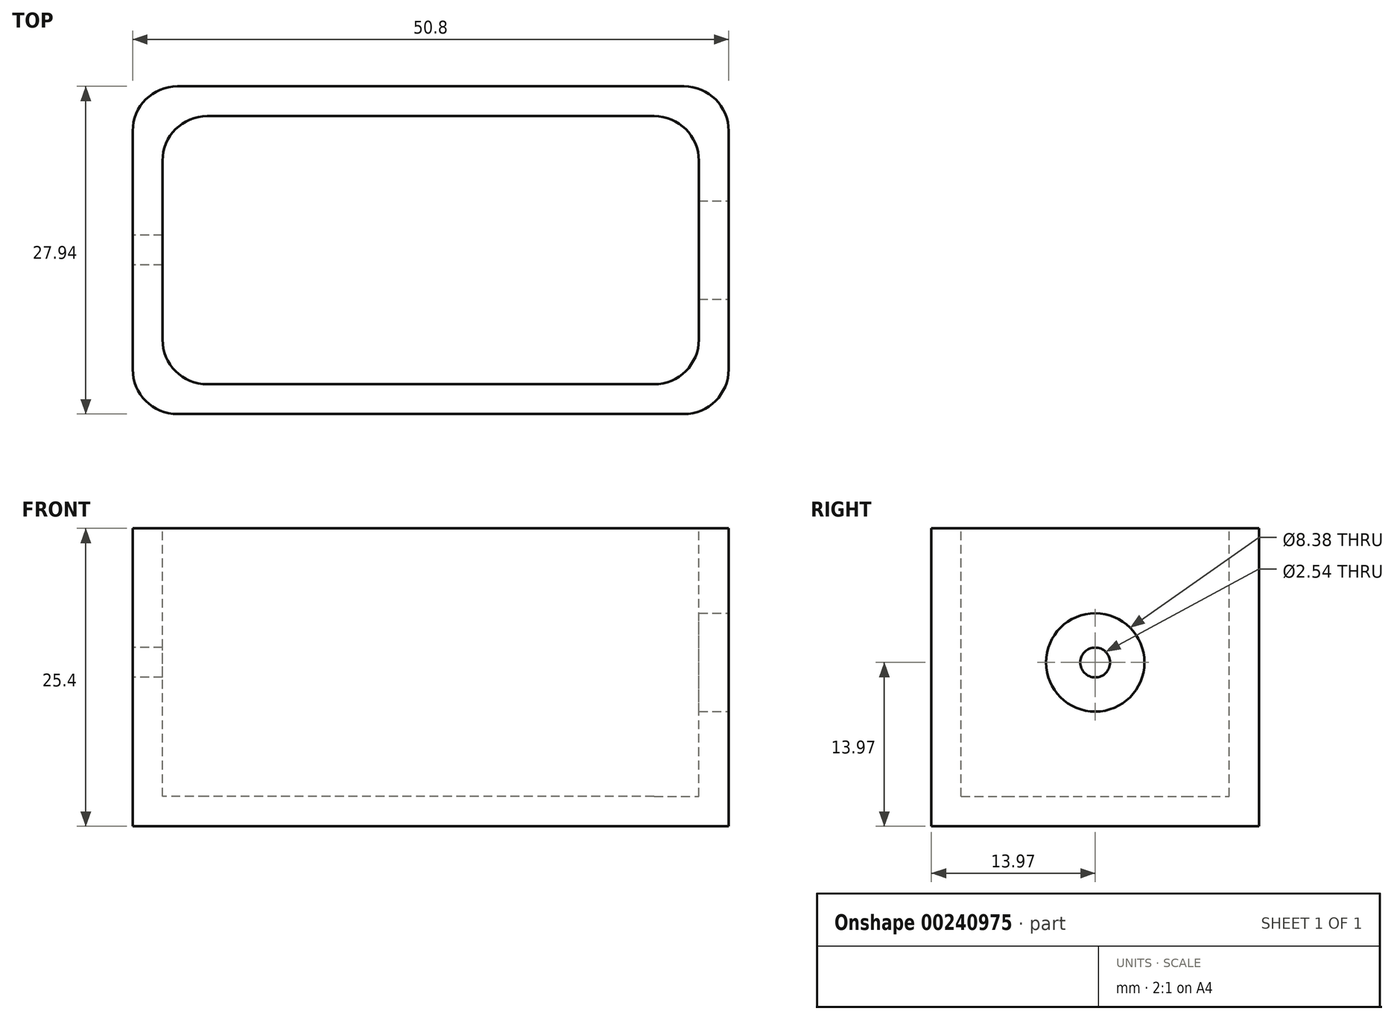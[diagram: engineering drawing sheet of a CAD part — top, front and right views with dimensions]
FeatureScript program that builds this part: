
annotation { "Feature Type Name" : "Feature", "Feature Type Description" : "" }
export const myFeature = defineFeature(function(context is Context, id is Id, definition is map)
    precondition{}
    {
        {
            var Q0;
            Q0=qCreatedBy(makeId("Top.planeOp"),FACE);
            var sketch = newSketch(context, id + "F0", { "sketchPlane" : qUnion([Q0])});
            skLineSegment(sketch, "E0.bottom", {"start": v(25.4, -13.97) * mm, "end": v(-25.4, -13.97) * mm});
            skLineSegment(sketch, "E0.top", {"start": v(25.4, 13.97) * mm, "end": v(-25.4, 13.97) * mm});
            skLineSegment(sketch, "E0.left", {"start": v(25.4, -13.97) * mm, "end": v(25.4, 13.97) * mm});
            skLineSegment(sketch, "E0.right", {"start": v(-25.4, -13.97) * mm, "end": v(-25.4, 13.97) * mm});
            skPoint(sketch, "E0.middle", {"position": v(0, 0) * mm});
            skSolve(sketch);
        }
        {
            var Q0;
            Q0=makeQuery(id+"F0.imprint","IMPRINT",FACE,{"disambiguationData":[TD([[makeQuery(id+"F0.imprint","IMPRINT",EDGE,{"derivedFrom":sQuery(id+"F0.wireOp",EDGE,"E0.bottom")}),-1.0]])]});
            extrude(context, id + "F1", {"entities" : qUnion([Q0]), "depth" : 25.4 * mm});
        }
        {
            var Q0;
            Q0=makeQuery(id+"F1.opExtrude","CAP_FACE",FACE,{"disambiguationData":[OSD([sQuery(id+"F0.wireOp",EDGE,"E0.bottom"),sQuery(id+"F0.wireOp",EDGE,"E0.top"),sQuery(id+"F0.wireOp",EDGE,"E0.left"),sQuery(id+"F0.wireOp",EDGE,"E0.right")])],"isStart":false});
            var sketch = newSketch(context, id + "F2", { "sketchPlane" : qUnion([Q0])});
            skLineSegment(sketch, "E1.bottom", {"start": v(22.86, -11.43) * mm, "end": v(-22.86, -11.43) * mm});
            skLineSegment(sketch, "E1.top", {"start": v(22.86, 11.43) * mm, "end": v(-22.86, 11.43) * mm});
            skLineSegment(sketch, "E1.left", {"start": v(22.86, -11.43) * mm, "end": v(22.86, 11.43) * mm});
            skLineSegment(sketch, "E1.right", {"start": v(-22.86, -11.43) * mm, "end": v(-22.86, 11.43) * mm});
            skPoint(sketch, "E1.middle", {"position": v(0, 0) * mm});
            skSolve(sketch);
        }
        {
            var Q0;
            Q0 = qSketchRegion(id + "F2", true);
            extrude(context, id + "F3", {"entities" : qUnion([Q0]), "operationType" : NewBodyOperationType.REMOVE, "oppositeDirection" : true, "depth" : 22.86 * mm});
        }
        {
            var Q0;
            Q0=makeQuery(id+"F1.opExtrude","SWEPT_EDGE",EDGE,{"disambiguationData":[OSD([sQuery(id+"F0.wireOp",EDGE,"E0.bottom"),sQuery(id+"F0.wireOp",EDGE,"E0.right")])]});
            var Q1;
            Q1=makeQuery(id+"F1.opExtrude","SWEPT_EDGE",EDGE,{"disambiguationData":[OSD([sQuery(id+"F0.wireOp",EDGE,"E0.bottom"),sQuery(id+"F0.wireOp",EDGE,"E0.left")])]});
            var Q2;
            Q2=makeQuery(id+"F1.opExtrude","SWEPT_EDGE",EDGE,{"disambiguationData":[OSD([sQuery(id+"F0.wireOp",EDGE,"E0.top"),sQuery(id+"F0.wireOp",EDGE,"E0.left")])]});
            var Q3;
            Q3=makeQuery(id+"F1.opExtrude","SWEPT_EDGE",EDGE,{"disambiguationData":[OSD([sQuery(id+"F0.wireOp",EDGE,"E0.top"),sQuery(id+"F0.wireOp",EDGE,"E0.right")])]});
            var Q4;
            Q4=makeQuery(id+"F3.boolean.opBoolean","COPY",EDGE,{"derivedFrom":makeQuery(id+"F3.opExtrude","SWEPT_EDGE",EDGE,{"disambiguationData":[OSD([sQuery(id+"F2.wireOp",EDGE,"E1.bottom"),sQuery(id+"F2.wireOp",EDGE,"E1.right")])]})});
            var Q5;
            Q5=makeQuery(id+"F3.boolean.opBoolean","COPY",EDGE,{"derivedFrom":makeQuery(id+"F3.opExtrude","SWEPT_EDGE",EDGE,{"disambiguationData":[OSD([sQuery(id+"F2.wireOp",EDGE,"E1.top"),sQuery(id+"F2.wireOp",EDGE,"E1.right")])]})});
            var Q6;
            Q6=makeQuery(id+"F3.boolean.opBoolean","COPY",EDGE,{"derivedFrom":makeQuery(id+"F3.opExtrude","SWEPT_EDGE",EDGE,{"disambiguationData":[OSD([sQuery(id+"F2.wireOp",EDGE,"E1.top"),sQuery(id+"F2.wireOp",EDGE,"E1.left")])]})});
            var Q7;
            Q7=makeQuery(id+"F3.boolean.opBoolean","COPY",EDGE,{"derivedFrom":makeQuery(id+"F3.opExtrude","SWEPT_EDGE",EDGE,{"disambiguationData":[OSD([sQuery(id+"F2.wireOp",EDGE,"E1.bottom"),sQuery(id+"F2.wireOp",EDGE,"E1.left")])]})});
            fillet(context, id + "F4", {"entities" : qUnion([Q0, Q1, Q2, Q3, Q4, Q5, Q6, Q7]), "radius" : 3.8 * mm, "tangentPropagation" : true, "allowEdgeOverflow" : false});
        }
        {
            var Q0;
            Q0=makeQuery(id+"F1.opExtrude","SWEPT_FACE",FACE,{"disambiguationData":[OSD([sQuery(id+"F0.wireOp",EDGE,"E0.left")])]});
            var sketch = newSketch(context, id + "F5", { "sketchPlane" : qUnion([Q0])});
            skLineSegment(sketch, "E2.0", {"start": v(-13.97, 0) * mm, "end": v(-13.97, 25.4) * mm});
            skLineSegment(sketch, "E3.0", {"start": v(13.97, 25.4) * mm, "end": v(13.97, 0) * mm});
            skLineSegment(sketch, "E4", {"start": v(-13.97, 13.97) * mm, "end": v(13.97, 13.97) * mm, "construction": true});
            skPoint(sketch, "E5", {"position": v(0, 13.97) * mm});
            skCircle(sketch, "E6", {"center": v(0, 13.97) * mm, "radius": 4.2 * mm});
            skSolve(sketch);
        }
        {
            var Q0;
            Q0 = qSketchRegion(id + "F5", true);
            extrude(context, id + "F6", {"entities" : qUnion([Q0]), "operationType" : NewBodyOperationType.REMOVE, "endBound" : BoundingType.UP_TO_NEXT, "oppositeDirection" : true, "depth" : 25.4 * mm});
        }
        {
            var Q0;
            Q0=makeQuery(id+"F1.opExtrude","SWEPT_FACE",FACE,{"disambiguationData":[OSD([sQuery(id+"F0.wireOp",EDGE,"E0.right")])]});
            var sketch = newSketch(context, id + "F7", { "sketchPlane" : qUnion([Q0])});
            skCircle(sketch, "E7.0", {"center": v(0, 13.97) * mm, "radius": 4.2 * mm, "construction": true});
            skCircle(sketch, "E8", {"center": v(0, 13.97) * mm, "radius": 1.27 * mm});
            skSolve(sketch);
        }
        {
            var Q0;
            Q0 = qSketchRegion(id + "F7", true);
            extrude(context, id + "F8", {"entities" : qUnion([Q0]), "operationType" : NewBodyOperationType.REMOVE, "endBound" : BoundingType.UP_TO_NEXT, "oppositeDirection" : true, "depth" : 25.4 * mm});
        }
    });
